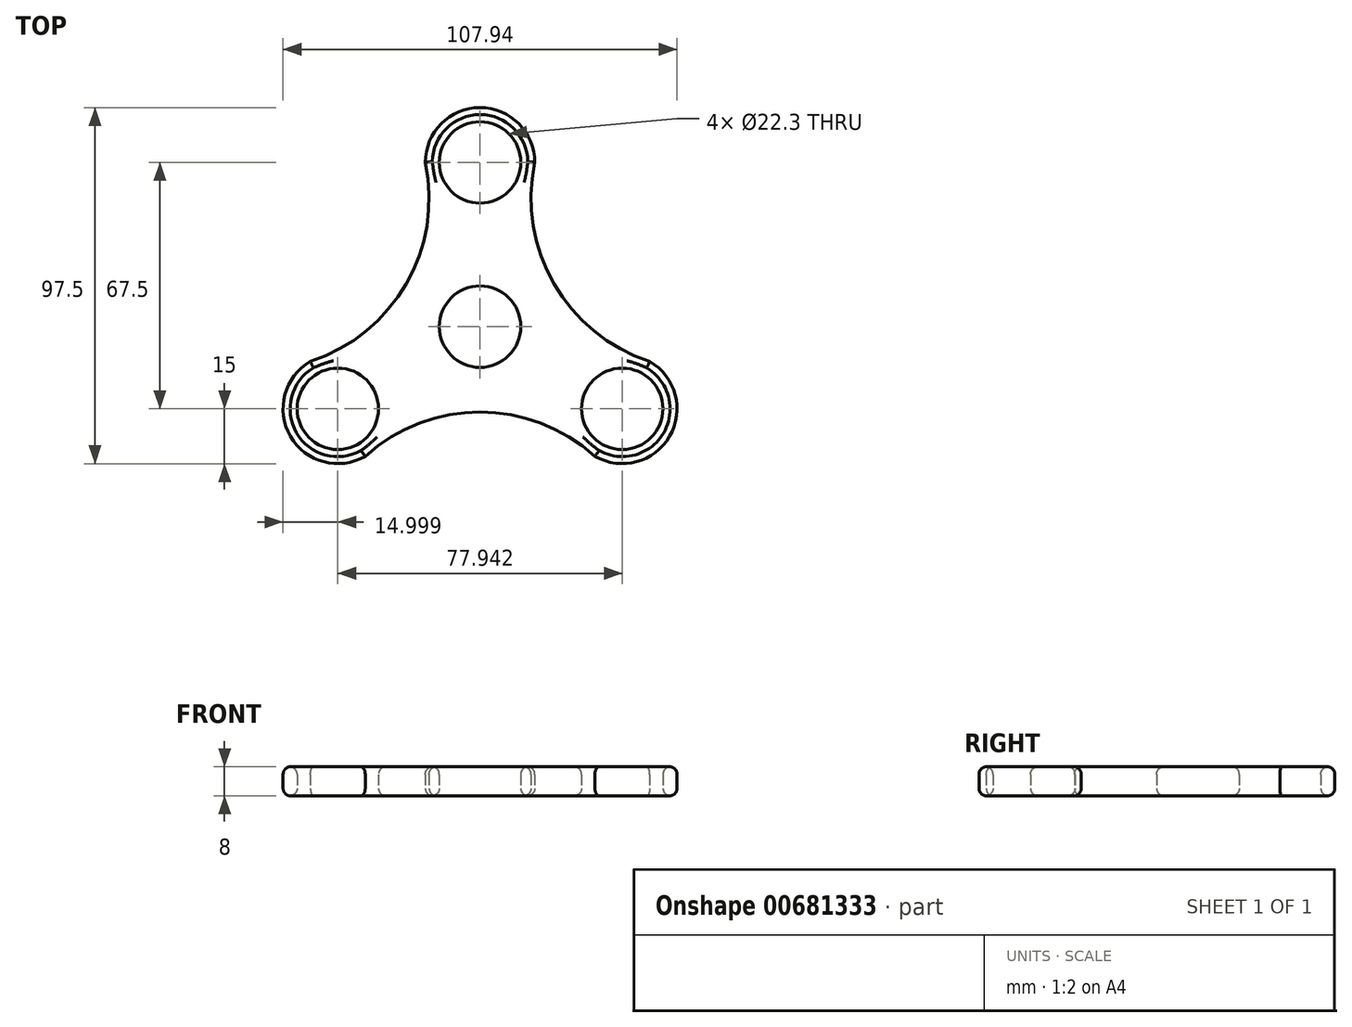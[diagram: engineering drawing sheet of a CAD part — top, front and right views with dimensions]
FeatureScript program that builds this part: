
annotation { "Feature Type Name" : "Feature", "Feature Type Description" : "" }
export const myFeature = defineFeature(function(context is Context, id is Id, definition is map)
    precondition{}
    {
        {
            var Q0;
            Q0=qCreatedBy(makeId("Top.planeOp"),FACE);
            var sketch = newSketch(context, id + "F0", { "sketchPlane" : qUnion([Q0])});
            skCircle(sketch, "E0", {"center": v(0, 0) * mm, "radius": 11.15 * mm});
            skPoint(sketch, "E1.0.midPoint", {"position": v(0, 17.25) * mm});
            skLineSegment(sketch, "E2", {"start": v(0, 0) * mm, "end": v(0, 60) * mm});
            skLineSegment(sketch, "E3", {"start": v(0, 0) * mm, "end": v(51.96, -30) * mm});
            skLineSegment(sketch, "E4", {"start": v(0, 0) * mm, "end": v(-51.96, -30) * mm});
            skCircle(sketch, "E5", {"center": v(0, 45) * mm, "radius": 15 * mm});
            skCircle(sketch, "E6", {"center": v(-38.97, -22.5) * mm, "radius": 15 * mm});
            skCircle(sketch, "E7", {"center": v(38.97, -22.5) * mm, "radius": 15 * mm});
            skLineSegment(sketch, "E8", {"start": v(0, 45) * mm, "end": v(-15, 45) * mm});
            skLineSegment(sketch, "E9", {"start": v(-15, 45) * mm, "end": v(15, 45) * mm});
            skLineSegment(sketch, "E10", {"start": v(-38.97, -22.5) * mm, "end": v(-46.47, -9.5) * mm});
            skLineSegment(sketch, "E11", {"start": v(-46.47, -9.5) * mm, "end": v(-31.47, -35.5) * mm});
            skLineSegment(sketch, "E12", {"start": v(38.97, -22.5) * mm, "end": v(46.47, -9.5) * mm});
            skLineSegment(sketch, "E13", {"start": v(46.47, -9.5) * mm, "end": v(31.47, -35.5) * mm});
            skArc(sketch, "E14", {"start": v(-46.47, -9.5) * mm, "mid": v(-20.26, 11.7) * mm, "end": v(-15, 45) * mm});
            skArc(sketch, "E15", {"start": v(15, 45) * mm, "mid": v(20.26, 11.7) * mm, "end": v(46.47, -9.5) * mm});
            skArc(sketch, "E16", {"start": v(31.47, -35.5) * mm, "mid": v(0, -23.4) * mm, "end": v(-31.47, -35.5) * mm});
            skCircle(sketch, "E17", {"center": v(0, 45) * mm, "radius": 11.15 * mm});
            skCircle(sketch, "E18", {"center": v(-38.97, -22.5) * mm, "radius": 11.15 * mm});
            skCircle(sketch, "E19", {"center": v(38.97, -22.5) * mm, "radius": 11.15 * mm});
            skSolve(sketch);
        }
        {
            var Q0;
            {var subQ3=sQuery(id+"F0.wireOp",EDGE,"E2");var subQ6=sQuery(id+"F0.wireOp",EDGE,"E0");var subQ10=makeQuery(id+"F0.imprint","INTERSECT",VERTEX,{"derivedFrom":[subQ6,subQ3]});Q0=makeQuery(id+"F0.imprint","IMPRINT",FACE,{"disambiguationData":[TD([[makeQuery(id+"F0.imprint","IMPRINT",EDGE,{"disambiguationData":[TD([[subQ10,1.0]])],"derivedFrom":subQ6}),-1.0]])]});}
            var Q1;
            {var subQ0=sQuery(id+"F0.wireOp",EDGE,"E4");var subQ1=sQuery(id+"F0.wireOp",EDGE,"E0");var subQ2=makeQuery(id+"F0.imprint","INTERSECT",VERTEX,{"derivedFrom":[subQ1,subQ0]});Q1=makeQuery(id+"F0.imprint","IMPRINT",FACE,{"disambiguationData":[TD([[makeQuery(id+"F0.imprint","IMPRINT",EDGE,{"disambiguationData":[TD([[subQ2,1.0]])],"derivedFrom":subQ1}),-1.0]])]});}
            var Q2;
            {var subQ3=sQuery(id+"F0.wireOp",EDGE,"E4");var subQ6=sQuery(id+"F0.wireOp",EDGE,"E0");var subQ10=makeQuery(id+"F0.imprint","INTERSECT",VERTEX,{"derivedFrom":[subQ6,subQ3]});Q2=makeQuery(id+"F0.imprint","IMPRINT",FACE,{"disambiguationData":[TD([[makeQuery(id+"F0.imprint","IMPRINT",EDGE,{"disambiguationData":[TD([[subQ10,-1.0]])],"derivedFrom":subQ6}),-1.0]])]});}
            var Q3;
            {var subQ0=sQuery(id+"F0.wireOp",EDGE,"E7");var subQ1=sQuery(id+"F0.wireOp",EDGE,"E3");var subQ2=makeQuery(id+"F0.imprint","INTERSECT",VERTEX,{"disambiguationData":[OD(0.0)],"derivedFrom":[subQ1,subQ0]});Q3=makeQuery(id+"F0.imprint","IMPRINT",FACE,{"disambiguationData":[TD([[makeQuery(id+"F0.imprint","IMPRINT",EDGE,{"disambiguationData":[TD([[subQ2,1.0]])],"derivedFrom":subQ1}),-1.0]])]});}
            var Q4;
            {var subQ2=sQuery(id+"F0.wireOp",EDGE,"E7");var subQ5=sQuery(id+"F0.wireOp",EDGE,"E3");var subQ6=makeQuery(id+"F0.imprint","INTERSECT",VERTEX,{"disambiguationData":[OD(1.0)],"derivedFrom":[subQ5,subQ2]});Q4=makeQuery(id+"F0.imprint","IMPRINT",FACE,{"disambiguationData":[TD([[makeQuery(id+"F0.imprint","IMPRINT",EDGE,{"disambiguationData":[TD([[subQ6,-1.0]])],"derivedFrom":subQ5}),-1.0]])]});}
            var Q5;
            {var subQ2=sQuery(id+"F0.wireOp",EDGE,"E7");var subQ7=sQuery(id+"F0.wireOp",EDGE,"E3");var subQ8=makeQuery(id+"F0.imprint","INTERSECT",VERTEX,{"disambiguationData":[OD(1.0)],"derivedFrom":[subQ7,subQ2]});Q5=makeQuery(id+"F0.imprint","IMPRINT",FACE,{"disambiguationData":[TD([[makeQuery(id+"F0.imprint","IMPRINT",EDGE,{"disambiguationData":[TD([[subQ8,-1.0]])],"derivedFrom":subQ7}),1.0]])]});}
            var Q6;
            {var subQ0=sQuery(id+"F0.wireOp",EDGE,"E7");var subQ1=sQuery(id+"F0.wireOp",EDGE,"E3");var subQ2=makeQuery(id+"F0.imprint","INTERSECT",VERTEX,{"disambiguationData":[OD(0.0)],"derivedFrom":[subQ1,subQ0]});Q6=makeQuery(id+"F0.imprint","IMPRINT",FACE,{"disambiguationData":[TD([[makeQuery(id+"F0.imprint","IMPRINT",EDGE,{"disambiguationData":[TD([[subQ2,1.0]])],"derivedFrom":subQ1}),1.0]])]});}
            var Q7;
            {var subQ2=sQuery(id+"F0.wireOp",EDGE,"E6");var subQ7=sQuery(id+"F0.wireOp",EDGE,"E4");var subQ8=makeQuery(id+"F0.imprint","INTERSECT",VERTEX,{"disambiguationData":[OD(1.0)],"derivedFrom":[subQ7,subQ2]});Q7=makeQuery(id+"F0.imprint","IMPRINT",FACE,{"disambiguationData":[TD([[makeQuery(id+"F0.imprint","IMPRINT",EDGE,{"disambiguationData":[TD([[subQ8,-1.0]])],"derivedFrom":subQ7}),1.0]])]});}
            var Q8;
            {var subQ0=sQuery(id+"F0.wireOp",EDGE,"E6");var subQ1=sQuery(id+"F0.wireOp",EDGE,"E4");var subQ2=makeQuery(id+"F0.imprint","INTERSECT",VERTEX,{"disambiguationData":[OD(0.0)],"derivedFrom":[subQ1,subQ0]});Q8=makeQuery(id+"F0.imprint","IMPRINT",FACE,{"disambiguationData":[TD([[makeQuery(id+"F0.imprint","IMPRINT",EDGE,{"disambiguationData":[TD([[subQ2,1.0]])],"derivedFrom":subQ1}),1.0]])]});}
            var Q9;
            {var subQ2=sQuery(id+"F0.wireOp",EDGE,"E6");var subQ7=sQuery(id+"F0.wireOp",EDGE,"E4");var subQ8=makeQuery(id+"F0.imprint","INTERSECT",VERTEX,{"disambiguationData":[OD(1.0)],"derivedFrom":[subQ7,subQ2]});Q9=makeQuery(id+"F0.imprint","IMPRINT",FACE,{"disambiguationData":[TD([[makeQuery(id+"F0.imprint","IMPRINT",EDGE,{"disambiguationData":[TD([[subQ8,-1.0]])],"derivedFrom":subQ7}),-1.0]])]});}
            var Q10;
            {var subQ0=sQuery(id+"F0.wireOp",EDGE,"E6");var subQ1=sQuery(id+"F0.wireOp",EDGE,"E4");var subQ2=makeQuery(id+"F0.imprint","INTERSECT",VERTEX,{"disambiguationData":[OD(0.0)],"derivedFrom":[subQ1,subQ0]});Q10=makeQuery(id+"F0.imprint","IMPRINT",FACE,{"disambiguationData":[TD([[makeQuery(id+"F0.imprint","IMPRINT",EDGE,{"disambiguationData":[TD([[subQ2,1.0]])],"derivedFrom":subQ1}),-1.0]])]});}
            var Q11;
            {var subQ2=sQuery(id+"F0.wireOp",EDGE,"E5");var subQ7=sQuery(id+"F0.wireOp",EDGE,"E2");var subQ8=makeQuery(id+"F0.imprint","INTERSECT",VERTEX,{"disambiguationData":[OD(1.0)],"derivedFrom":[subQ7,subQ2]});Q11=makeQuery(id+"F0.imprint","IMPRINT",FACE,{"disambiguationData":[TD([[makeQuery(id+"F0.imprint","IMPRINT",EDGE,{"disambiguationData":[TD([[subQ8,-1.0]])],"derivedFrom":subQ7}),1.0]])]});}
            var Q12;
            {var subQ2=sQuery(id+"F0.wireOp",EDGE,"E5");var subQ7=sQuery(id+"F0.wireOp",EDGE,"E2");var subQ8=makeQuery(id+"F0.imprint","INTERSECT",VERTEX,{"disambiguationData":[OD(1.0)],"derivedFrom":[subQ7,subQ2]});Q12=makeQuery(id+"F0.imprint","IMPRINT",FACE,{"disambiguationData":[TD([[makeQuery(id+"F0.imprint","IMPRINT",EDGE,{"disambiguationData":[TD([[subQ8,-1.0]])],"derivedFrom":subQ7}),-1.0]])]});}
            var Q13;
            {var subQ0=sQuery(id+"F0.wireOp",EDGE,"E5");var subQ1=sQuery(id+"F0.wireOp",EDGE,"E2");var subQ2=makeQuery(id+"F0.imprint","INTERSECT",VERTEX,{"disambiguationData":[OD(0.0)],"derivedFrom":[subQ1,subQ0]});Q13=makeQuery(id+"F0.imprint","IMPRINT",FACE,{"disambiguationData":[TD([[makeQuery(id+"F0.imprint","IMPRINT",EDGE,{"disambiguationData":[TD([[subQ2,1.0]])],"derivedFrom":subQ1}),-1.0]])]});}
            var Q14;
            {var subQ0=sQuery(id+"F0.wireOp",EDGE,"E5");var subQ1=sQuery(id+"F0.wireOp",EDGE,"E2");var subQ2=makeQuery(id+"F0.imprint","INTERSECT",VERTEX,{"disambiguationData":[OD(0.0)],"derivedFrom":[subQ1,subQ0]});Q14=makeQuery(id+"F0.imprint","IMPRINT",FACE,{"disambiguationData":[TD([[makeQuery(id+"F0.imprint","IMPRINT",EDGE,{"disambiguationData":[TD([[subQ2,1.0]])],"derivedFrom":subQ1}),1.0]])]});}
            extrude(context, id + "F1", {"entities" : qUnion([Q0, Q1, Q2, Q3, Q4, Q5, Q6, Q7, Q8, Q9, Q10, Q11, Q12, Q13, Q14]), "depth" : 8 * mm, "offsetDistance" : 25 * mm});
        }
        {
            var Q0;
            Q0=makeQuery(id+"F1.opExtrude","CAP_FACE",FACE,{"disambiguationData":[OSD([sQuery(id+"F0.wireOp",EDGE,"E0"),sQuery(id+"F0.wireOp",EDGE,"E5"),sQuery(id+"F0.wireOp",EDGE,"E6"),sQuery(id+"F0.wireOp",EDGE,"E7"),sQuery(id+"F0.wireOp",EDGE,"E14"),sQuery(id+"F0.wireOp",EDGE,"E15"),sQuery(id+"F0.wireOp",EDGE,"E16"),sQuery(id+"F0.wireOp",EDGE,"E17"),sQuery(id+"F0.wireOp",EDGE,"E18"),sQuery(id+"F0.wireOp",EDGE,"E19")])],"isStart":false});
            var Q1;
            Q1=makeQuery(id+"F1.opExtrude","CAP_EDGE",EDGE,{"disambiguationData":[OSD([sQuery(id+"F0.wireOp",EDGE,"E15")])],"isStart":false});
            fillet(context, id + "F2", {"entities" : qUnion([Q0, Q1]), "radius" : 2.1 * mm, "tangentPropagation" : true, "allowEdgeOverflow" : false});
        }
        {
            var Q0;
            Q0=makeQuery(id+"F1.opExtrude","CAP_FACE",FACE,{"disambiguationData":[OSD([sQuery(id+"F0.wireOp",EDGE,"E0"),sQuery(id+"F0.wireOp",EDGE,"E5"),sQuery(id+"F0.wireOp",EDGE,"E6"),sQuery(id+"F0.wireOp",EDGE,"E7"),sQuery(id+"F0.wireOp",EDGE,"E14"),sQuery(id+"F0.wireOp",EDGE,"E15"),sQuery(id+"F0.wireOp",EDGE,"E16"),sQuery(id+"F0.wireOp",EDGE,"E17"),sQuery(id+"F0.wireOp",EDGE,"E18"),sQuery(id+"F0.wireOp",EDGE,"E19")])],"isStart":true});
            fillet(context, id + "F3", {"entities" : qUnion([Q0]), "radius" : 2.1 * mm, "tangentPropagation" : true, "allowEdgeOverflow" : false});
        }
    });
